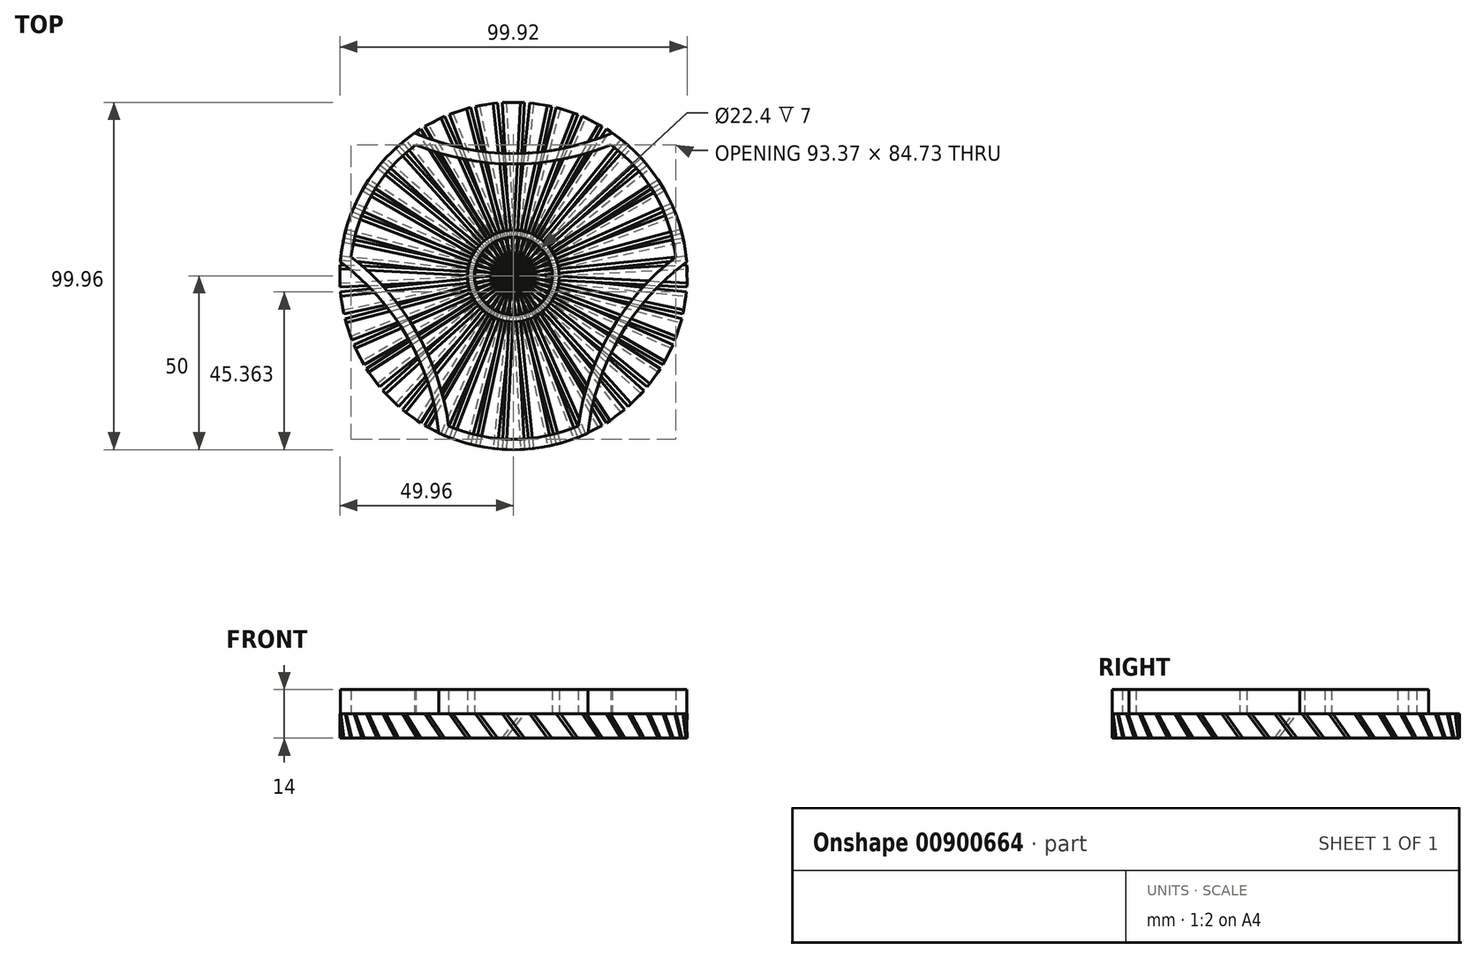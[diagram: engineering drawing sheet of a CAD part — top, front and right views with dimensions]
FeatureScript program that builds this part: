
annotation { "Feature Type Name" : "Feature", "Feature Type Description" : "" }
export const myFeature = defineFeature(function(context is Context, id is Id, definition is map)
    precondition{}
    {
        {
            var Q0;
            Q0=qCreatedBy(makeId("Top.planeOp"),FACE);
            var sketch = newSketch(context, id + "F0", { "sketchPlane" : qUnion([Q0])});
            skLineSegment(sketch, "E0.bottom", {"start": v(-3.22, 49.9) * mm, "end": v(-2.02, 49.96) * mm});
            skLineSegment(sketch, "E0.top", {"start": v(2.02, -49.96) * mm, "end": v(3.22, -49.9) * mm});
            skLineSegment(sketch, "E0.left", {"start": v(-3.22, 49.9) * mm, "end": v(2.02, -49.96) * mm});
            skLineSegment(sketch, "E0.right", {"start": v(-2.02, 49.96) * mm, "end": v(3.22, -49.9) * mm});
            skPoint(sketch, "E0.middle", {"position": v(0, 0) * mm});
            skSolve(sketch);
        }
        {
            var Q0;
            Q0=qCreatedBy(makeId("Top.planeOp"),FACE);
            cPlane(context, id + "F1", {"entities" : qUnion([Q0]), "cplaneType" : CPlaneType.OFFSET, "offset" : 7 * mm, "width" : 150 * mm, "height" : 150 * mm});
        }
        {
            var Q0;
            Q0=qCreatedBy(id+"F1.planeOp",FACE);
            var sketch = newSketch(context, id + "F2", { "sketchPlane" : qUnion([Q0])});
            skLineSegment(sketch, "E1.bottom", {"start": v(3.22, 49.9) * mm, "end": v(2.02, 49.96) * mm});
            skLineSegment(sketch, "E1.top", {"start": v(-2.02, -49.96) * mm, "end": v(-3.22, -49.9) * mm});
            skLineSegment(sketch, "E1.left", {"start": v(3.22, 49.9) * mm, "end": v(-2.02, -49.96) * mm});
            skLineSegment(sketch, "E1.right", {"start": v(2.02, 49.96) * mm, "end": v(-3.22, -49.9) * mm});
            skPoint(sketch, "E1.middle", {"position": v(0, 0) * mm});
            skSolve(sketch);
        }
        {
            var Q0;
            Q0=makeQuery(id+"F0.imprint","IMPRINT",FACE,{"disambiguationData":[TD([[makeQuery(id+"F0.imprint","IMPRINT",EDGE,{"derivedFrom":sQuery(id+"F0.wireOp",EDGE,"E0.bottom")}),-1.0]])]});
            var Q1;
            Q1=makeQuery(id+"F2.imprint","IMPRINT",FACE,{"disambiguationData":[TD([[makeQuery(id+"F2.imprint","IMPRINT",EDGE,{"derivedFrom":sQuery(id+"F2.wireOp",EDGE,"E1.bottom")}),1.0]])]});
            loft(context, id + "F3", {"sheetProfilesArray" : [{ "sheetProfileEntities" : qUnion([Q0]) }, { "sheetProfileEntities" : qUnion([Q1]) }]});
        }
        {
            var Q0;
            Q0=qCreatedBy(makeId("Right.planeOp"),FACE);
            var sketch = newSketch(context, id + "F4", { "sketchPlane" : qUnion([Q0])});
            skLineSegment(sketch, "E2", {"start": v(0, 0) * mm, "end": v(0, 30.98) * mm});
            skSolve(sketch);
        }
        {
            var Q0;
            Q0=makeQuery(id+"F3.opLoft","SWEPT_BODY",BODY,{"disambiguationData":[OSD([makeQuery(id+"F0.imprint","IMPRINT",FACE,{"disambiguationData":[TD([[makeQuery(id+"F0.imprint","IMPRINT",EDGE,{"derivedFrom":sQuery(id+"F0.wireOp",EDGE,"E0.bottom")}),-1.0]])]}),makeQuery(id+"F2.imprint","IMPRINT",FACE,{"disambiguationData":[TD([[makeQuery(id+"F2.imprint","IMPRINT",EDGE,{"derivedFrom":sQuery(id+"F2.wireOp",EDGE,"E1.bottom")}),1.0]])]})])]});
            var Q1;
            Q1=sQuery(id+"F4.wireOp",EDGE,"E2");
            circularPattern(context, id + "F5", {"entities" : qUnion([Q0]), "axis" : qUnion([Q1]), "angle" : 360 * degree, "instanceCount" : 40, "equalSpace" : true});
        }
        {
            var Q0;
            Q0=qCreatedBy(id+"F1.planeOp",FACE);
            var sketch = newSketch(context, id + "F6", { "sketchPlane" : qUnion([Q0])});
            skArc(sketch, "E3", {"start": v(49.84, 4.03) * mm, "mid": v(43.3, 25) * mm, "end": v(28.41, 41.14) * mm});
            skLineSegment(sketch, "E4", {"start": v(-28.41, 41.14) * mm, "end": v(28.41, 41.14) * mm, "construction": true});
            skArc(sketch, "E5", {"start": v(-28.41, 41.14) * mm, "mid": v(0, 35.22) * mm, "end": v(28.41, 41.14) * mm});
            skArc(sketch, "E6.1.0", {"start": v(-21.43, -45.18) * mm, "mid": v(-30.5, -17.61) * mm, "end": v(-49.84, 4.03) * mm});
            skArc(sketch, "E6.2.0", {"start": v(49.84, 4.03) * mm, "mid": v(30.5, -17.61) * mm, "end": v(21.43, -45.18) * mm});
            skArc(sketch, "E7.trimOffspring", {"start": v(-21.43, -45.18) * mm, "mid": v(0, -50) * mm, "end": v(21.43, -45.18) * mm});
            skArc(sketch, "E8.trimOffspring", {"start": v(-28.41, 41.14) * mm, "mid": v(-43.3, 25) * mm, "end": v(-49.84, 4.03) * mm});
            skArc(sketch, "E9.0", {"start": v(-28.03, 37.73) * mm, "mid": v(0, 32.22) * mm, "end": v(28.03, 37.73) * mm});
            skArc(sketch, "E9.1", {"start": v(-18.66, -43.14) * mm, "mid": v(-27.9, -16.11) * mm, "end": v(-46.69, 5.41) * mm});
            skArc(sketch, "E9.2", {"start": v(-18.66, -43.14) * mm, "mid": v(0, -47) * mm, "end": v(18.66, -43.14) * mm});
            skArc(sketch, "E9.3", {"start": v(-28.03, 37.73) * mm, "mid": v(-40.7, 23.5) * mm, "end": v(-46.69, 5.41) * mm});
            skArc(sketch, "E9.4", {"start": v(46.69, 5.41) * mm, "mid": v(27.9, -16.11) * mm, "end": v(18.66, -43.14) * mm});
            skArc(sketch, "E9.5", {"start": v(46.69, 5.41) * mm, "mid": v(40.7, 23.5) * mm, "end": v(28.03, 37.73) * mm});
            skCircle(sketch, "E10", {"center": v(0, 0) * mm, "radius": 11.2 * mm});
            skCircle(sketch, "E11", {"center": v(0, 0) * mm, "radius": 13.2 * mm});
            skSolve(sketch);
        }
        {
            var Q0;
            Q0=makeQuery(id+"F6.imprint","IMPRINT",FACE,{"disambiguationData":[TD([[makeQuery(id+"F6.imprint","IMPRINT",EDGE,{"derivedFrom":sQuery(id+"F6.wireOp",EDGE,"E10")}),-1.0]])]});
            var Q1;
            Q1=makeQuery(id+"F6.imprint","IMPRINT",FACE,{"disambiguationData":[TD([[makeQuery(id+"F6.imprint","IMPRINT",EDGE,{"derivedFrom":sQuery(id+"F6.wireOp",EDGE,"E3")}),1.0]])]});
            extrude(context, id + "F7", {"entities" : qUnion([Q0, Q1]), "depth" : 7 * mm, "offsetDistance" : 25 * mm});
        }
    });
